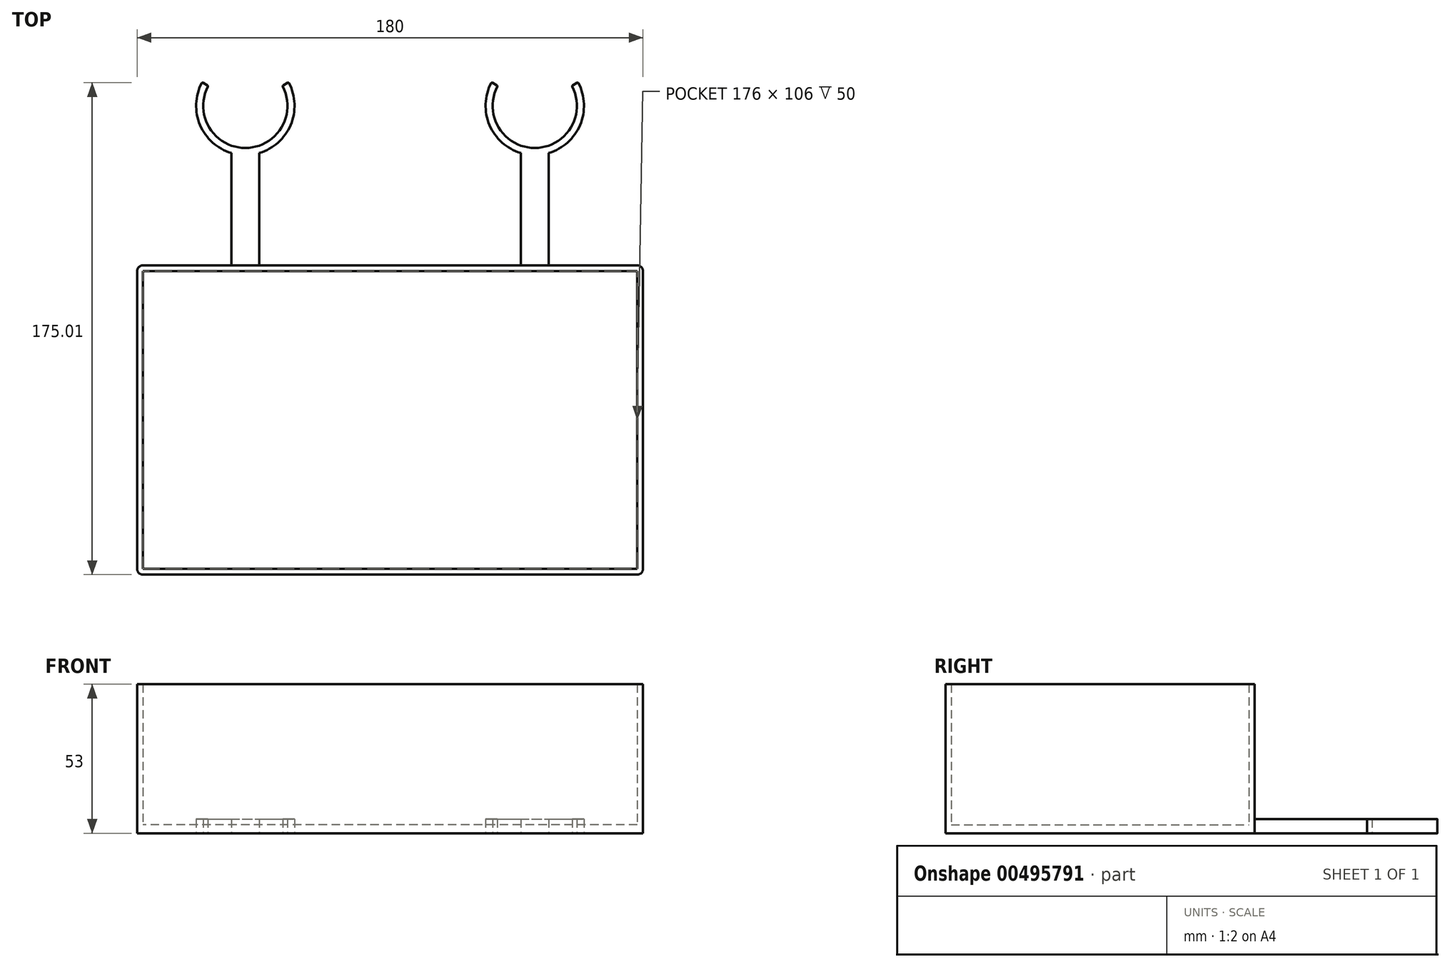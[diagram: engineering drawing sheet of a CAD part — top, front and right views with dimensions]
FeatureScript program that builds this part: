
annotation { "Feature Type Name" : "Feature", "Feature Type Description" : "" }
export const myFeature = defineFeature(function(context is Context, id is Id, definition is map)
    precondition{}
    {
        {
            var Q0;
            Q0=qCreatedBy(makeId("Top.planeOp"),FACE);
            var sketch = newSketch(context, id + "F0", { "sketchPlane" : qUnion([Q0])});
            skLineSegment(sketch, "E0.bottom", {"start": v(88, -55) * mm, "end": v(-88, -55) * mm});
            skLineSegment(sketch, "E0.top", {"start": v(88, 55) * mm, "end": v(-88, 55) * mm});
            skLineSegment(sketch, "E0.left", {"start": v(90, -53) * mm, "end": v(90, 53) * mm});
            skLineSegment(sketch, "E0.right", {"start": v(-90, -53) * mm, "end": v(-90, 53) * mm});
            skPoint(sketch, "E0.middle", {"position": v(0, 0) * mm});
            skLineSegment(sketch, "E1", {"start": v(-56.5, 55) * mm, "end": v(-56.5, 95) * mm});
            skLineSegment(sketch, "E2", {"start": v(-46.5, 55) * mm, "end": v(-46.5, 95) * mm});
            skLineSegment(sketch, "E3", {"start": v(46.5, 55) * mm, "end": v(46.5, 95) * mm});
            skLineSegment(sketch, "E4", {"start": v(56.5, 55) * mm, "end": v(56.5, 95) * mm});
            skArc(sketch, "E5", {"start": v(-64.84, 118.62) * mm, "mid": v(-51.5, 96.77) * mm, "end": v(-38.16, 118.62) * mm});
            skArc(sketch, "E6", {"start": v(38.17, 118.64) * mm, "mid": v(51.5, 96.77) * mm, "end": v(64.84, 118.63) * mm});
            skLineSegment(sketch, "E7", {"start": v(-51.5, 55) * mm, "end": v(-51.5, -55) * mm, "construction": true});
            skLineSegment(sketch, "E8", {"start": v(51.5, 55) * mm, "end": v(51.5, -55) * mm, "construction": true});
            skArc(sketch, "E9", {"start": v(-67.02, 119.85) * mm, "mid": v(-51.5, 94.27) * mm, "end": v(-35.98, 119.85) * mm});
            skArc(sketch, "E10", {"start": v(35.98, 119.85) * mm, "mid": v(51.5, 94.27) * mm, "end": v(67.02, 119.85) * mm});
            skLineSegment(sketch, "E11", {"start": v(-66.6, 119.97) * mm, "end": v(-64.96, 119.02) * mm});
            skLineSegment(sketch, "E12", {"start": v(-36.4, 119.97) * mm, "end": v(-38.04, 119.02) * mm});
            skLineSegment(sketch, "E13", {"start": v(36.4, 119.97) * mm, "end": v(38.05, 119.04) * mm});
            skLineSegment(sketch, "E14", {"start": v(66.88, 120.13) * mm, "end": v(64.7, 118.89) * mm});
            skLineSegment(sketch, "E15", {"start": v(66.6, 119.97) * mm, "end": v(64.96, 119.03) * mm});
            skPoint(sketch, "E16.visualSharp", {"position": v(-90, 55) * mm});
            skArc(sketch, "E16.filletArc", {"start": v(-88, 55) * mm, "mid": v(-89.41, 54.41) * mm, "end": v(-90, 53) * mm});
            skPoint(sketch, "E17.visualSharp", {"position": v(-90, -55) * mm});
            skArc(sketch, "E17.filletArc", {"start": v(-90, -53) * mm, "mid": v(-89.41, -54.41) * mm, "end": v(-88, -55) * mm});
            skPoint(sketch, "E18.visualSharp", {"position": v(90, 55) * mm});
            skArc(sketch, "E18.filletArc", {"start": v(90, 53) * mm, "mid": v(89.41, 54.41) * mm, "end": v(88, 55) * mm});
            skPoint(sketch, "E19.visualSharp", {"position": v(90, -55) * mm});
            skArc(sketch, "E19.filletArc", {"start": v(88, -55) * mm, "mid": v(89.41, -54.41) * mm, "end": v(90, -53) * mm});
            skPoint(sketch, "E20.visualSharp", {"position": v(64.7, 118.89) * mm});
            skArc(sketch, "E20.filletArc", {"start": v(64.96, 119.03) * mm, "mid": v(64.82, 118.86) * mm, "end": v(64.84, 118.63) * mm});
            skPoint(sketch, "E21.visualSharp", {"position": v(66.88, 120.13) * mm});
            skArc(sketch, "E21.filletArc", {"start": v(67.02, 119.85) * mm, "mid": v(66.84, 120) * mm, "end": v(66.6, 119.97) * mm});
            skPoint(sketch, "E22.visualSharp", {"position": v(38.3, 118.9) * mm});
            skArc(sketch, "E22.filletArc", {"start": v(38.17, 118.64) * mm, "mid": v(38.19, 118.87) * mm, "end": v(38.05, 119.04) * mm});
            skPoint(sketch, "E23.visualSharp", {"position": v(36.12, 120.12) * mm});
            skArc(sketch, "E23.filletArc", {"start": v(36.4, 119.97) * mm, "mid": v(36.16, 120) * mm, "end": v(35.98, 119.85) * mm});
            skPoint(sketch, "E24.visualSharp", {"position": v(-38.3, 118.88) * mm});
            skArc(sketch, "E24.filletArc", {"start": v(-38.04, 119.02) * mm, "mid": v(-38.18, 118.85) * mm, "end": v(-38.16, 118.62) * mm});
            skPoint(sketch, "E25.visualSharp", {"position": v(-36.12, 120.13) * mm});
            skArc(sketch, "E25.filletArc", {"start": v(-35.98, 119.85) * mm, "mid": v(-36.16, 120) * mm, "end": v(-36.4, 119.97) * mm});
            skPoint(sketch, "E26.visualSharp", {"position": v(-64.7, 118.88) * mm});
            skArc(sketch, "E26.filletArc", {"start": v(-64.84, 118.62) * mm, "mid": v(-64.82, 118.85) * mm, "end": v(-64.96, 119.02) * mm});
            skPoint(sketch, "E27.visualSharp", {"position": v(-66.88, 120.13) * mm});
            skArc(sketch, "E27.filletArc", {"start": v(-66.6, 119.97) * mm, "mid": v(-66.84, 120) * mm, "end": v(-67.02, 119.85) * mm});
            skSolve(sketch);
        }
        {
            var Q0;
            Q0=makeQuery(id+"F0.imprint","IMPRINT",FACE,{"disambiguationData":[TD([[makeQuery(id+"F0.imprint","IMPRINT",EDGE,{"derivedFrom":sQuery(id+"F0.wireOp",EDGE,"E5")}),-1.0]])]});
            var Q1;
            {var subQ0=sQuery(id+"F0.wireOp",EDGE,"E1");Q1=makeQuery(id+"F0.imprint","IMPRINT",FACE,{"disambiguationData":[TD([[makeQuery(id+"F0.imprint","IMPRINT",EDGE,{"derivedFrom":subQ0}),-1.0]])]});}
            var Q2;
            {var subQ0=sQuery(id+"F0.wireOp",EDGE,"E3");Q2=makeQuery(id+"F0.imprint","IMPRINT",FACE,{"disambiguationData":[TD([[makeQuery(id+"F0.imprint","IMPRINT",EDGE,{"derivedFrom":subQ0}),-1.0]])]});}
            var Q3;
            Q3=makeQuery(id+"F0.imprint","IMPRINT",FACE,{"disambiguationData":[TD([[makeQuery(id+"F0.imprint","IMPRINT",EDGE,{"derivedFrom":sQuery(id+"F0.wireOp",EDGE,"E0.bottom")}),-1.0]])]});
            var Q4;
            Q4=makeQuery(id+"F0.imprint","IMPRINT",FACE,{"disambiguationData":[TD([[makeQuery(id+"F0.imprint","IMPRINT",EDGE,{"derivedFrom":sQuery(id+"F0.wireOp",EDGE,"E6")}),-1.0]])]});
            extrude(context, id + "F1", {"entities" : qUnion([Q0, Q1, Q2, Q3, Q4]), "depth" : 3 * mm});
        }
        {
            var Q0;
            Q0=makeQuery(id+"F1.opExtrude","CAP_FACE",FACE,{"disambiguationData":[OSD([sQuery(id+"F0.wireOp",EDGE,"E0.bottom"),sQuery(id+"F0.wireOp",EDGE,"E0.top"),sQuery(id+"F0.wireOp",EDGE,"E0.left"),sQuery(id+"F0.wireOp",EDGE,"E0.right"),sQuery(id+"F0.wireOp",EDGE,"E1"),sQuery(id+"F0.wireOp",EDGE,"E2"),sQuery(id+"F0.wireOp",EDGE,"E3"),sQuery(id+"F0.wireOp",EDGE,"E4"),sQuery(id+"F0.wireOp",EDGE,"E5"),sQuery(id+"F0.wireOp",EDGE,"E6"),sQuery(id+"F0.wireOp",EDGE,"E9"),sQuery(id+"F0.wireOp",EDGE,"E10"),sQuery(id+"F0.wireOp",EDGE,"E11"),sQuery(id+"F0.wireOp",EDGE,"E12"),sQuery(id+"F0.wireOp",EDGE,"E13"),sQuery(id+"F0.wireOp",EDGE,"E15")])],"isStart":false});
            var sketch = newSketch(context, id + "F2", { "sketchPlane" : qUnion([Q0])});
            skLineSegment(sketch, "E28", {"start": v(-56.5, 55) * mm, "end": v(-46.5, 55) * mm});
            skLineSegment(sketch, "E29", {"start": v(46.5, 55) * mm, "end": v(56.5, 55) * mm});
            skLineSegment(sketch, "E30.0", {"start": v(-56.5, 53) * mm, "end": v(-88, 53) * mm});
            skLineSegment(sketch, "E30.1", {"start": v(-88, -53) * mm, "end": v(-88, 53) * mm});
            skLineSegment(sketch, "E30.2", {"start": v(-56.5, 53) * mm, "end": v(-46.5, 53) * mm});
            skLineSegment(sketch, "E30.3", {"start": v(88, -53) * mm, "end": v(-88, -53) * mm});
            skLineSegment(sketch, "E30.4", {"start": v(46.5, 53) * mm, "end": v(-46.5, 53) * mm});
            skLineSegment(sketch, "E30.5", {"start": v(46.5, 53) * mm, "end": v(56.5, 53) * mm});
            skLineSegment(sketch, "E30.6", {"start": v(88, 53) * mm, "end": v(56.5, 53) * mm});
            skLineSegment(sketch, "E30.7", {"start": v(88, -53) * mm, "end": v(88, 53) * mm});
            skSolve(sketch);
        }
        {
            var Q0;
            Q0=makeQuery(id+"F2.imprint","IMPRINT",FACE,{"disambiguationData":[TD([[makeQuery(id+"F2.imprint","IMPRINT",EDGE,{"derivedFrom":sQuery(id+"F2.wireOp",EDGE,"E28")}),-1.0]])]});
            extrude(context, id + "F3", {"entities" : qUnion([Q0]), "operationType" : NewBodyOperationType.ADD, "depth" : 50 * mm});
        }
        {
            var Q0;
            {var subQ0=sQuery(id+"F0.wireOp",EDGE,"E13");var subQ1=sQuery(id+"F0.wireOp",EDGE,"E10");var subQ2=sQuery(id+"F0.wireOp",EDGE,"E4");var subQ3=sQuery(id+"F0.wireOp",EDGE,"E21.filletArc");var subQ4=sQuery(id+"F0.wireOp",EDGE,"E6");var subQ5=sQuery(id+"F0.wireOp",EDGE,"E18.filletArc");var subQ6=sQuery(id+"F0.wireOp",EDGE,"E0.top");var subQ7=sQuery(id+"F0.wireOp",EDGE,"E20.filletArc");var subQ8=sQuery(id+"F0.wireOp",EDGE,"E2");var subQ9=sQuery(id+"F0.wireOp",EDGE,"E3");var subQ10=sQuery(id+"F0.wireOp",EDGE,"E23.filletArc");var subQ11=sQuery(id+"F0.wireOp",EDGE,"E16.filletArc");var subQ12=sQuery(id+"F0.wireOp",EDGE,"E1");var subQ13=sQuery(id+"F0.wireOp",EDGE,"E22.filletArc");var subQ14=sQuery(id+"F0.wireOp",EDGE,"E15");Q0=makeQuery(id+"F3.boolean.opBoolean","SPLIT",FACE,{"disambiguationData":[TD([makeQuery(id+"F1.opExtrude","SWEPT_FACE",FACE,{"disambiguationData":[OSD([subQ9])]})])],"derivedFrom":makeQuery(id+"F1.opExtrude","CAP_FACE",FACE,{"disambiguationData":[OSD([sQuery(id+"F0.wireOp",EDGE,"E0.bottom"),subQ6,sQuery(id+"F0.wireOp",EDGE,"E0.left"),sQuery(id+"F0.wireOp",EDGE,"E0.right"),subQ12,subQ8,subQ9,subQ2,sQuery(id+"F0.wireOp",EDGE,"E5"),subQ4,sQuery(id+"F0.wireOp",EDGE,"E9"),subQ1,sQuery(id+"F0.wireOp",EDGE,"E11"),sQuery(id+"F0.wireOp",EDGE,"E12"),subQ0,subQ14,subQ11,sQuery(id+"F0.wireOp",EDGE,"E17.filletArc"),subQ5,sQuery(id+"F0.wireOp",EDGE,"E19.filletArc"),subQ7,subQ3,subQ13,subQ10,sQuery(id+"F0.wireOp",EDGE,"E24.filletArc"),sQuery(id+"F0.wireOp",EDGE,"E25.filletArc"),sQuery(id+"F0.wireOp",EDGE,"E26.filletArc"),sQuery(id+"F0.wireOp",EDGE,"E27.filletArc")])],"isStart":false})});}
            var Q1;
            {var subQ0=sQuery(id+"F0.wireOp",EDGE,"E11");var subQ1=sQuery(id+"F0.wireOp",EDGE,"E5");var subQ2=sQuery(id+"F0.wireOp",EDGE,"E2");var subQ3=sQuery(id+"F0.wireOp",EDGE,"E26.filletArc");var subQ4=sQuery(id+"F0.wireOp",EDGE,"E9");var subQ5=sQuery(id+"F0.wireOp",EDGE,"E1");var subQ6=sQuery(id+"F0.wireOp",EDGE,"E27.filletArc");var subQ7=sQuery(id+"F0.wireOp",EDGE,"E18.filletArc");var subQ8=sQuery(id+"F0.wireOp",EDGE,"E0.top");var subQ9=sQuery(id+"F0.wireOp",EDGE,"E4");var subQ10=sQuery(id+"F0.wireOp",EDGE,"E12");var subQ11=sQuery(id+"F0.wireOp",EDGE,"E25.filletArc");var subQ12=sQuery(id+"F0.wireOp",EDGE,"E3");var subQ13=sQuery(id+"F0.wireOp",EDGE,"E16.filletArc");var subQ14=sQuery(id+"F0.wireOp",EDGE,"E24.filletArc");Q1=makeQuery(id+"F3.boolean.opBoolean","SPLIT",FACE,{"disambiguationData":[TD([makeQuery(id+"F1.opExtrude","SWEPT_FACE",FACE,{"disambiguationData":[OSD([subQ5])]})])],"derivedFrom":makeQuery(id+"F1.opExtrude","CAP_FACE",FACE,{"disambiguationData":[OSD([sQuery(id+"F0.wireOp",EDGE,"E0.bottom"),subQ8,sQuery(id+"F0.wireOp",EDGE,"E0.left"),sQuery(id+"F0.wireOp",EDGE,"E0.right"),subQ5,subQ2,subQ12,subQ9,subQ1,sQuery(id+"F0.wireOp",EDGE,"E6"),subQ4,sQuery(id+"F0.wireOp",EDGE,"E10"),subQ0,subQ10,sQuery(id+"F0.wireOp",EDGE,"E13"),sQuery(id+"F0.wireOp",EDGE,"E15"),subQ13,sQuery(id+"F0.wireOp",EDGE,"E17.filletArc"),subQ7,sQuery(id+"F0.wireOp",EDGE,"E19.filletArc"),sQuery(id+"F0.wireOp",EDGE,"E20.filletArc"),sQuery(id+"F0.wireOp",EDGE,"E21.filletArc"),sQuery(id+"F0.wireOp",EDGE,"E22.filletArc"),sQuery(id+"F0.wireOp",EDGE,"E23.filletArc"),subQ14,subQ11,subQ3,subQ6])],"isStart":false})});}
            extrude(context, id + "F4", {"entities" : qUnion([Q0, Q1]), "operationType" : NewBodyOperationType.ADD, "depth" : 2 * mm});
        }
        {
            var Q0;
            Q0=qCreatedBy(makeId("Front.planeOp"),FACE);
            var sketch = newSketch(context, id + "F5", { "sketchPlane" : qUnion([Q0])});
            skCircle(sketch, "E31", {"center": v(0, 185) * mm, "radius": 65 * mm});
            skSolve(sketch);
        }
        {
            var Q0;
            Q0=makeQuery(id+"F5.imprint","IMPRINT",FACE,{"disambiguationData":[TD([[makeQuery(id+"F5.imprint","IMPRINT",EDGE,{"derivedFrom":sQuery(id+"F5.wireOp",EDGE,"E31")}),1.0]])]});
            extrude(context, id + "F6", {"entities" : qUnion([Q0]), "operationType" : NewBodyOperationType.REMOVE, "endBound" : BoundingType.THROUGH_ALL, "oppositeDirection" : true, "depth" : 25 * mm, "hasSecondDirection" : true, "secondDirectionOppositeDirection" : false, "secondDirectionDepth" : 70 * mm});
        }
    });
